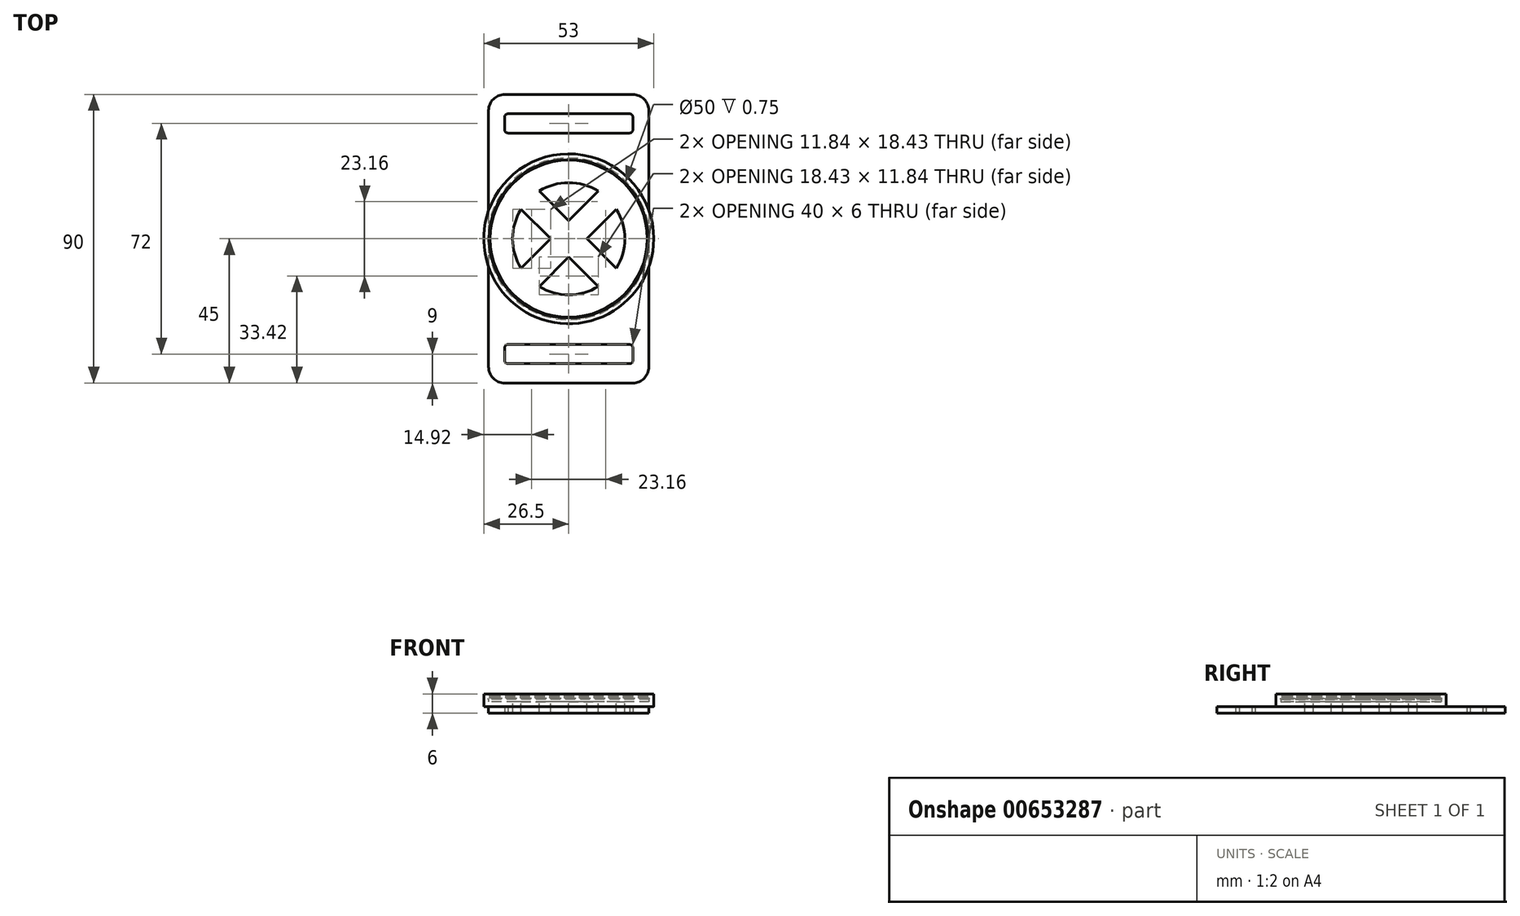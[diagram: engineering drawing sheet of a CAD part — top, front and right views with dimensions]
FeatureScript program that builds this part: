
annotation { "Feature Type Name" : "Feature", "Feature Type Description" : "" }
export const myFeature = defineFeature(function(context is Context, id is Id, definition is map)
    precondition{}
    {
        {
            var Q0;
            Q0=qCreatedBy(makeId("Top.planeOp"),FACE);
            var sketch = newSketch(context, id + "F0", { "sketchPlane" : qUnion([Q0])});
            skLineSegment(sketch, "E0.bottom", {"start": v(-25, 45) * mm, "end": v(25, 45) * mm});
            skLineSegment(sketch, "E0.top", {"start": v(-25, -45) * mm, "end": v(25, -45) * mm});
            skLineSegment(sketch, "E0.left", {"start": v(-25, 45) * mm, "end": v(-25, -45) * mm});
            skLineSegment(sketch, "E0.right", {"start": v(25, 45) * mm, "end": v(25, -45) * mm});
            skLineSegment(sketch, "E1", {"start": v(-25, 0) * mm, "end": v(25, 0) * mm, "construction": true});
            skLineSegment(sketch, "E2", {"start": v(0, -45) * mm, "end": v(0, 45) * mm, "construction": true});
            skPoint(sketch, "E3", {"position": v(0, 0) * mm});
            skSolve(sketch);
        }
        {
            var Q0;
            Q0=qSketchRegion(id+"F0",true);
            extrude(context, id + "F1", {"entities" : qUnion([Q0]), "depth" : 2 * mm, "offsetDistance" : 25 * mm});
        }
        {
            var Q0;
            Q0=makeQuery(id+"F1.opExtrude","CAP_FACE",FACE,{"disambiguationData":[OSD([sQuery(id+"F0.wireOp",EDGE,"E0.bottom"),sQuery(id+"F0.wireOp",EDGE,"E0.top"),sQuery(id+"F0.wireOp",EDGE,"E0.left"),sQuery(id+"F0.wireOp",EDGE,"E0.right")])],"isStart":false});
            var sketch = newSketch(context, id + "F2", { "sketchPlane" : qUnion([Q0])});
            skCircle(sketch, "E4", {"center": v(0, 0) * mm, "radius": 26.5 * mm});
            skSolve(sketch);
        }
        {
            var Q0;
            Q0=qSketchRegion(id+"F2",true);
            extrude(context, id + "F3", {"entities" : qUnion([Q0]), "operationType" : NewBodyOperationType.ADD, "depth" : 1.5 * mm, "offsetDistance" : 25 * mm});
        }
        {
            var Q0;
            Q0=makeQuery(id+"F3.opExtrude","CAP_FACE",FACE,{"disambiguationData":[OSD([sQuery(id+"F2.wireOp",EDGE,"E4")])],"isStart":false});
            var sketch = newSketch(context, id + "F4", { "sketchPlane" : qUnion([Q0])});
            skCircle(sketch, "E5", {"center": v(0, 0) * mm, "radius": 25 * mm});
            skSolve(sketch);
        }
        {
            var Q0;
            Q0=makeQuery(id+"F4.imprint","IMPRINT",FACE,{"disambiguationData":[TD([[makeQuery(id+"F4.imprint","IMPRINT",EDGE,{"derivedFrom":sQuery(id+"F4.wireOp",EDGE,"E5")}),-1.0]])]});
            extrude(context, id + "F5", {"entities" : qUnion([Q0]), "operationType" : NewBodyOperationType.ADD, "depth" : 1 * mm, "offsetDistance" : 25 * mm});
        }
        {
            var Q0;
            Q0=makeQuery(id+"F1.opExtrude","CAP_FACE",FACE,{"disambiguationData":[OSD([sQuery(id+"F0.wireOp",EDGE,"E0.bottom"),sQuery(id+"F0.wireOp",EDGE,"E0.top"),sQuery(id+"F0.wireOp",EDGE,"E0.left"),sQuery(id+"F0.wireOp",EDGE,"E0.right")])],"isStart":true});
            var sketch = newSketch(context, id + "F6", { "sketchPlane" : qUnion([Q0])});
            skLineSegment(sketch, "E6.bottom", {"start": v(-25, 35) * mm, "end": v(-22, 35) * mm});
            skLineSegment(sketch, "E6.top", {"start": v(-25, -35) * mm, "end": v(-22, -35) * mm});
            skLineSegment(sketch, "E6.left", {"start": v(-25, 35) * mm, "end": v(-25, -35) * mm});
            skLineSegment(sketch, "E6.right", {"start": v(-22, 35) * mm, "end": v(-22, -35) * mm});
            skLineSegment(sketch, "E7.bottom", {"start": v(22, 35) * mm, "end": v(25, 35) * mm});
            skLineSegment(sketch, "E7.top", {"start": v(22, -35) * mm, "end": v(25, -35) * mm});
            skLineSegment(sketch, "E7.left", {"start": v(22, 35) * mm, "end": v(22, -35) * mm});
            skLineSegment(sketch, "E7.right", {"start": v(25, 35) * mm, "end": v(25, -35) * mm});
            skSolve(sketch);
        }
        {
            var Q0;
            Q0=makeQuery(id+"F6.imprint","IMPRINT",FACE,{"disambiguationData":[TD([[makeQuery(id+"F6.imprint","IMPRINT",EDGE,{"derivedFrom":sQuery(id+"F6.wireOp",EDGE,"E6.bottom")}),-1.0]])]});
            var Q1;
            Q1=makeQuery(id+"F6.imprint","IMPRINT",FACE,{"disambiguationData":[TD([[makeQuery(id+"F6.imprint","IMPRINT",EDGE,{"derivedFrom":sQuery(id+"F6.wireOp",EDGE,"E7.bottom")}),-1.0]])]});
            extrude(context, id + "F7", {"entities" : qUnion([Q0, Q1]), "operationType" : NewBodyOperationType.ADD, "depth" : 3 * mm, "offsetDistance" : 25 * mm});
        }
        {
            var Q0;
            {var subQ0=sQuery(id+"F6.wireOp",EDGE,"E6.right");var subQ2=sQuery(id+"F6.wireOp",EDGE,"E6.left");var subQ3=sQuery(id+"F6.wireOp",EDGE,"E6.top");Q0=makeQuery(id+"Fcp3DyhTEGZhcjd_1.boolean.opBoolean","SPLIT",FACE,{"disambiguationData":[TD([makeQuery(id+"F7.opExtrude","SWEPT_FACE",FACE,{"disambiguationData":[OSD([subQ3])]})])],"derivedFrom":makeQuery(id+"F7.opExtrude","CAP_FACE",FACE,{"disambiguationData":[OSD([sQuery(id+"F6.wireOp",EDGE,"E6.bottom"),subQ3,subQ2,subQ0])],"isStart":false})});}
            var Q1;
            {var subQ0=sQuery(id+"F6.wireOp",EDGE,"E7.right");var subQ1=sQuery(id+"F6.wireOp",EDGE,"E7.left");var subQ2=sQuery(id+"F6.wireOp",EDGE,"E7.top");Q1=makeQuery(id+"Fcp3DyhTEGZhcjd_1.boolean.opBoolean","SPLIT",FACE,{"disambiguationData":[TD([makeQuery(id+"F7.opExtrude","SWEPT_FACE",FACE,{"disambiguationData":[OSD([subQ2])]})])],"derivedFrom":makeQuery(id+"F7.opExtrude","CAP_FACE",FACE,{"disambiguationData":[OSD([sQuery(id+"F6.wireOp",EDGE,"E7.bottom"),subQ2,subQ1,subQ0])],"isStart":false})});}
            var Q2;
            {var subQ0=sQuery(id+"F6.wireOp",EDGE,"E6.left");var subQ1=sQuery(id+"F6.wireOp",EDGE,"E6.right");var subQ3=sQuery(id+"F6.wireOp",EDGE,"E6.bottom");Q2=makeQuery(id+"Fcp3DyhTEGZhcjd_1.boolean.opBoolean","SPLIT",FACE,{"disambiguationData":[TD([makeQuery(id+"F7.opExtrude","SWEPT_FACE",FACE,{"disambiguationData":[OSD([subQ3])]})])],"derivedFrom":makeQuery(id+"F7.opExtrude","CAP_FACE",FACE,{"disambiguationData":[OSD([subQ3,sQuery(id+"F6.wireOp",EDGE,"E6.top"),subQ0,subQ1])],"isStart":false})});}
            var Q3;
            {var subQ0=sQuery(id+"F6.wireOp",EDGE,"E7.left");var subQ1=sQuery(id+"F6.wireOp",EDGE,"E7.right");var subQ2=sQuery(id+"F6.wireOp",EDGE,"E7.bottom");Q3=makeQuery(id+"Fcp3DyhTEGZhcjd_1.boolean.opBoolean","SPLIT",FACE,{"disambiguationData":[TD([makeQuery(id+"F7.opExtrude","SWEPT_FACE",FACE,{"disambiguationData":[OSD([subQ2])]})])],"derivedFrom":makeQuery(id+"F7.opExtrude","CAP_FACE",FACE,{"disambiguationData":[OSD([subQ2,sQuery(id+"F6.wireOp",EDGE,"E7.top"),subQ0,subQ1])],"isStart":false})});}
            var Q4;
            Q4=makeQuery(id+"F1.opExtrude","CAP_FACE",FACE,{"disambiguationData":[OSD([sQuery(id+"F0.wireOp",EDGE,"E0.bottom"),sQuery(id+"F0.wireOp",EDGE,"E0.top"),sQuery(id+"F0.wireOp",EDGE,"E0.left"),sQuery(id+"F0.wireOp",EDGE,"E0.right")])],"isStart":true});
            extrude(context, id + "F8", {"entities" : qUnion([Q0, Q1, Q2, Q3]), "operationType" : NewBodyOperationType.REMOVE, "endBound" : BoundingType.UP_TO_SURFACE, "oppositeDirection" : true, "depth" : 25 * mm, "endBoundEntityFace" : qUnion([Q4]), "offsetDistance" : 25 * mm});
        }
        {
            var Q0;
            Q0=makeQuery(id+"F3.opExtrude","CAP_FACE",FACE,{"disambiguationData":[OSD([sQuery(id+"F2.wireOp",EDGE,"E4")])],"isStart":false});
            var sketch = newSketch(context, id + "F9", { "sketchPlane" : qUnion([Q0])});
            skCircle(sketch, "E8", {"center": v(0, 0) * mm, "radius": 17.5 * mm});
            skLineSegment(sketch, "E9", {"start": v(14.88, -9.22) * mm, "end": v(5.66, 0) * mm});
            skLineSegment(sketch, "E10", {"start": v(-14.88, 9.22) * mm, "end": v(-5.66, 0) * mm});
            skLineSegment(sketch, "E11", {"start": v(14.88, 9.22) * mm, "end": v(5.66, 0) * mm});
            skLineSegment(sketch, "E12", {"start": v(-14.88, -9.22) * mm, "end": v(-5.66, 0) * mm});
            skLineSegment(sketch, "E13.trimOffspring", {"start": v(0, -5.66) * mm, "end": v(9.22, -14.88) * mm});
            skLineSegment(sketch, "E14.trimOffspring", {"start": v(0, 5.66) * mm, "end": v(9.22, 14.88) * mm});
            skLineSegment(sketch, "E15.trimOffspring", {"start": v(0, 5.66) * mm, "end": v(-9.22, 14.88) * mm});
            skLineSegment(sketch, "E16.trimOffspring", {"start": v(0, -5.66) * mm, "end": v(-9.22, -14.88) * mm});
            skLineSegment(sketch, "E17", {"start": v(0, 5.66) * mm, "end": v(0, 0) * mm, "construction": true});
            skLineSegment(sketch, "E18", {"start": v(-5.66, 0) * mm, "end": v(0, 0) * mm, "construction": true});
            skLineSegment(sketch, "E19", {"start": v(5.66, 0) * mm, "end": v(0, 0) * mm, "construction": true});
            skLineSegment(sketch, "E20", {"start": v(0, 0) * mm, "end": v(0, -5.66) * mm, "construction": true});
            skSolve(sketch);
        }
        {
            var Q0;
            {var subQ0=sQuery(id+"F9.wireOp",EDGE,"E10");Q0=makeQuery(id+"F9.imprint","IMPRINT",FACE,{"disambiguationData":[TD([[makeQuery(id+"F9.imprint","IMPRINT",EDGE,{"derivedFrom":subQ0}),-1.0]])]});}
            var Q1;
            {var subQ0=sQuery(id+"F9.wireOp",EDGE,"E13.trimOffspring");Q1=makeQuery(id+"F9.imprint","IMPRINT",FACE,{"disambiguationData":[TD([[makeQuery(id+"F9.imprint","IMPRINT",EDGE,{"derivedFrom":subQ0}),-1.0]])]});}
            var Q2;
            {var subQ0=sQuery(id+"F9.wireOp",EDGE,"E9");Q2=makeQuery(id+"F9.imprint","IMPRINT",FACE,{"disambiguationData":[TD([[makeQuery(id+"F9.imprint","IMPRINT",EDGE,{"derivedFrom":subQ0}),-1.0]])]});}
            var Q3;
            {var subQ0=sQuery(id+"F9.wireOp",EDGE,"E14.trimOffspring");Q3=makeQuery(id+"F9.imprint","IMPRINT",FACE,{"disambiguationData":[TD([[makeQuery(id+"F9.imprint","IMPRINT",EDGE,{"derivedFrom":subQ0}),1.0]])]});}
            extrude(context, id + "F10", {"entities" : qUnion([Q0, Q1, Q2, Q3]), "operationType" : NewBodyOperationType.REMOVE, "oppositeDirection" : true, "depth" : 25 * mm, "offsetDistance" : 25 * mm});
        }
        {
            var Q0;
            {var subQ0=sQuery(id+"F0.wireOp",EDGE,"E0.right");var subQ1=sQuery(id+"F0.wireOp",EDGE,"E0.left");var subQ2=sQuery(id+"F0.wireOp",EDGE,"E0.top");var subQ3=sQuery(id+"F0.wireOp",EDGE,"E0.bottom");Q0=makeQuery(id+"F8.boolean.opBoolean","MERGE",FACE,{"derivedFrom":[makeQuery(id+"F1.opExtrude","CAP_FACE",FACE,{"disambiguationData":[OSD([subQ3,subQ2,subQ1,subQ0])],"isStart":true}),makeQuery(id+"F8.opExtrude","CAP_FACE",FACE,{"disambiguationData":[OSD([subQ3,subQ2,subQ1,subQ0]),OD(0.0)],"isStart":false}),makeQuery(id+"F8.opExtrude","CAP_FACE",FACE,{"disambiguationData":[OSD([subQ3,subQ2,subQ1,subQ0]),OD(1.0)],"isStart":false}),makeQuery(id+"F8.opExtrude","CAP_FACE",FACE,{"disambiguationData":[OSD([subQ3,subQ2,subQ1,subQ0]),OD(2.0)],"isStart":false}),makeQuery(id+"F8.opExtrude","CAP_FACE",FACE,{"disambiguationData":[OSD([subQ3,subQ2,subQ1,subQ0]),OD(3.0)],"isStart":false})]});}
            var sketch = newSketch(context, id + "F11", { "sketchPlane" : qUnion([Q0])});
            skLineSegment(sketch, "E21.bottom", {"start": v(19, 39) * mm, "end": v(-19, 39) * mm});
            skLineSegment(sketch, "E21.top", {"start": v(19, 33) * mm, "end": v(-19, 33) * mm});
            skLineSegment(sketch, "E21.left", {"start": v(20, 38) * mm, "end": v(20, 34) * mm});
            skLineSegment(sketch, "E21.right", {"start": v(-20, 38) * mm, "end": v(-20, 34) * mm});
            skLineSegment(sketch, "E22.bottom", {"start": v(19, -33) * mm, "end": v(-19, -33) * mm});
            skLineSegment(sketch, "E22.top", {"start": v(19, -39) * mm, "end": v(-19, -39) * mm});
            skLineSegment(sketch, "E22.left", {"start": v(20, -34) * mm, "end": v(20, -38) * mm});
            skLineSegment(sketch, "E22.right", {"start": v(-20, -34) * mm, "end": v(-20, -38) * mm});
            skPoint(sketch, "E23.visualSharp", {"position": v(20, 39) * mm});
            skArc(sketch, "E23.filletArc", {"start": v(20, 38) * mm, "mid": v(19.7, 38.7) * mm, "end": v(19, 39) * mm});
            skPoint(sketch, "E24.visualSharp", {"position": v(20, 33) * mm});
            skArc(sketch, "E24.filletArc", {"start": v(19, 33) * mm, "mid": v(19.7, 33.3) * mm, "end": v(20, 34) * mm});
            skPoint(sketch, "E25.visualSharp", {"position": v(-20, 33) * mm});
            skArc(sketch, "E25.filletArc", {"start": v(-20, 34) * mm, "mid": v(-19.7, 33.3) * mm, "end": v(-19, 33) * mm});
            skPoint(sketch, "E26.visualSharp", {"position": v(-20, 39) * mm});
            skArc(sketch, "E26.filletArc", {"start": v(-19, 39) * mm, "mid": v(-19.7, 38.7) * mm, "end": v(-20, 38) * mm});
            skPoint(sketch, "E27.visualSharp", {"position": v(-20, -33) * mm});
            skArc(sketch, "E27.filletArc", {"start": v(-19, -33) * mm, "mid": v(-19.7, -33.3) * mm, "end": v(-20, -34) * mm});
            skPoint(sketch, "E28.visualSharp", {"position": v(-20, -39) * mm});
            skArc(sketch, "E28.filletArc", {"start": v(-20, -38) * mm, "mid": v(-19.7, -38.7) * mm, "end": v(-19, -39) * mm});
            skPoint(sketch, "E29.visualSharp", {"position": v(20, -39) * mm});
            skArc(sketch, "E29.filletArc", {"start": v(19, -39) * mm, "mid": v(19.7, -38.7) * mm, "end": v(20, -38) * mm});
            skPoint(sketch, "E30.visualSharp", {"position": v(20, -33) * mm});
            skArc(sketch, "E30.filletArc", {"start": v(20, -34) * mm, "mid": v(19.7, -33.3) * mm, "end": v(19, -33) * mm});
            skLineSegment(sketch, "E31.bottom", {"start": v(-4, 39) * mm, "end": v(4, 39) * mm});
            skLineSegment(sketch, "E31.top", {"start": v(-4, 45) * mm, "end": v(4, 45) * mm});
            skLineSegment(sketch, "E31.left", {"start": v(-4, 39) * mm, "end": v(-4, 45) * mm});
            skLineSegment(sketch, "E31.right", {"start": v(4, 39) * mm, "end": v(4, 45) * mm});
            skLineSegment(sketch, "E32.bottom", {"start": v(4, -39) * mm, "end": v(-4, -39) * mm});
            skLineSegment(sketch, "E32.top", {"start": v(4, -45) * mm, "end": v(-4, -45) * mm});
            skLineSegment(sketch, "E32.left", {"start": v(4, -39) * mm, "end": v(4, -45) * mm});
            skLineSegment(sketch, "E32.right", {"start": v(-4, -39) * mm, "end": v(-4, -45) * mm});
            skSolve(sketch);
        }
        {
            var Q0;
            Q0=makeQuery(id+"F11.imprint","IMPRINT",FACE,{"disambiguationData":[TD([[makeQuery(id+"F11.imprint","IMPRINT",EDGE,{"derivedFrom":sQuery(id+"F11.wireOp",EDGE,"E32.bottom")}),1.0]])]});
            var Q1;
            Q1=makeQuery(id+"F11.imprint","IMPRINT",FACE,{"disambiguationData":[TD([[makeQuery(id+"F11.imprint","IMPRINT",EDGE,{"derivedFrom":sQuery(id+"F11.wireOp",EDGE,"E22.bottom")}),1.0]])]});
            var Q2;
            Q2=makeQuery(id+"F11.imprint","IMPRINT",FACE,{"disambiguationData":[TD([[makeQuery(id+"F11.imprint","IMPRINT",EDGE,{"derivedFrom":sQuery(id+"F11.wireOp",EDGE,"E31.bottom")}),1.0]])]});
            var Q3;
            Q3=makeQuery(id+"F11.imprint","IMPRINT",FACE,{"disambiguationData":[TD([[makeQuery(id+"F11.imprint","IMPRINT",EDGE,{"derivedFrom":sQuery(id+"F11.wireOp",EDGE,"E21.top")}),-1.0]])]});
            extrude(context, id + "F12", {"entities" : qUnion([Q0, Q1, Q2, Q3]), "operationType" : NewBodyOperationType.REMOVE, "oppositeDirection" : true, "depth" : 25 * mm, "offsetDistance" : 25 * mm});
        }
        {
            var Q0;
            Q0=makeQuery(id+"F12.boolean.opBoolean","COPY",EDGE,{"derivedFrom":makeQuery(id+"F12.opExtrude","SWEPT_EDGE",EDGE,{"disambiguationData":[OSD([sQuery(id+"F0.wireOp",EDGE,"E0.top"),sQuery(id+"F11.wireOp",EDGE,"E31.top"),sQuery(id+"F11.wireOp",EDGE,"E31.left")])]})});
            var Q1;
            Q1=makeQuery(id+"F12.boolean.opBoolean","COPY",EDGE,{"derivedFrom":makeQuery(id+"F12.opExtrude","SWEPT_EDGE",EDGE,{"disambiguationData":[OSD([sQuery(id+"F11.wireOp",EDGE,"E21.bottom"),sQuery(id+"F11.wireOp",EDGE,"E31.bottom"),sQuery(id+"F11.wireOp",EDGE,"E31.left")])]})});
            var Q2;
            Q2=makeQuery(id+"F12.boolean.opBoolean","COPY",EDGE,{"derivedFrom":makeQuery(id+"F12.opExtrude","SWEPT_EDGE",EDGE,{"disambiguationData":[OSD([sQuery(id+"F0.wireOp",EDGE,"E0.top"),sQuery(id+"F11.wireOp",EDGE,"E31.top"),sQuery(id+"F11.wireOp",EDGE,"E31.right")])]})});
            var Q3;
            Q3=makeQuery(id+"F12.boolean.opBoolean","COPY",EDGE,{"derivedFrom":makeQuery(id+"F12.opExtrude","SWEPT_EDGE",EDGE,{"disambiguationData":[OSD([sQuery(id+"F11.wireOp",EDGE,"E21.bottom"),sQuery(id+"F11.wireOp",EDGE,"E31.bottom"),sQuery(id+"F11.wireOp",EDGE,"E31.right")])]})});
            fillet(context, id + "F13", {"entities" : qUnion([Q0, Q1, Q2, Q3]), "radius" : 1 * mm, "tangentPropagation" : true, "allowEdgeOverflow" : false});
        }
        {
            var Q0;
            Q0=makeQuery(id+"F12.boolean.opBoolean","COPY",EDGE,{"derivedFrom":makeQuery(id+"F12.opExtrude","SWEPT_EDGE",EDGE,{"disambiguationData":[OSD([sQuery(id+"F0.wireOp",EDGE,"E0.bottom"),sQuery(id+"F11.wireOp",EDGE,"E32.top"),sQuery(id+"F11.wireOp",EDGE,"E32.left")])]})});
            var Q1;
            Q1=makeQuery(id+"F12.boolean.opBoolean","COPY",EDGE,{"derivedFrom":makeQuery(id+"F12.opExtrude","SWEPT_EDGE",EDGE,{"disambiguationData":[OSD([sQuery(id+"F11.wireOp",EDGE,"E22.top"),sQuery(id+"F11.wireOp",EDGE,"E32.bottom"),sQuery(id+"F11.wireOp",EDGE,"E32.left")])]})});
            var Q2;
            Q2=makeQuery(id+"F12.boolean.opBoolean","COPY",EDGE,{"derivedFrom":makeQuery(id+"F12.opExtrude","SWEPT_EDGE",EDGE,{"disambiguationData":[OSD([sQuery(id+"F0.wireOp",EDGE,"E0.bottom"),sQuery(id+"F11.wireOp",EDGE,"E32.top"),sQuery(id+"F11.wireOp",EDGE,"E32.right")])]})});
            var Q3;
            Q3=makeQuery(id+"F12.boolean.opBoolean","COPY",EDGE,{"derivedFrom":makeQuery(id+"F12.opExtrude","SWEPT_EDGE",EDGE,{"disambiguationData":[OSD([sQuery(id+"F11.wireOp",EDGE,"E22.top"),sQuery(id+"F11.wireOp",EDGE,"E32.bottom"),sQuery(id+"F11.wireOp",EDGE,"E32.right")])]})});
            fillet(context, id + "F14", {"entities" : qUnion([Q0, Q1, Q2, Q3]), "radius" : 1 * mm, "tangentPropagation" : true, "allowEdgeOverflow" : false});
        }
        {
            var Q0;
            Q0=makeQuery(id+"F1.opExtrude","SWEPT_EDGE",EDGE,{"disambiguationData":[OSD([sQuery(id+"F0.wireOp",EDGE,"E0.top"),sQuery(id+"F0.wireOp",EDGE,"E0.right")])]});
            var Q1;
            Q1=makeQuery(id+"F1.opExtrude","SWEPT_EDGE",EDGE,{"disambiguationData":[OSD([sQuery(id+"F0.wireOp",EDGE,"E0.bottom"),sQuery(id+"F0.wireOp",EDGE,"E0.right")])]});
            var Q2;
            Q2=makeQuery(id+"F1.opExtrude","SWEPT_EDGE",EDGE,{"disambiguationData":[OSD([sQuery(id+"F0.wireOp",EDGE,"E0.bottom"),sQuery(id+"F0.wireOp",EDGE,"E0.left")])]});
            var Q3;
            Q3=makeQuery(id+"F1.opExtrude","SWEPT_EDGE",EDGE,{"disambiguationData":[OSD([sQuery(id+"F0.wireOp",EDGE,"E0.top"),sQuery(id+"F0.wireOp",EDGE,"E0.left")])]});
            fillet(context, id + "F15", {"entities" : qUnion([Q0, Q1, Q2, Q3]), "radius" : 5 * mm, "tangentPropagation" : true, "allowEdgeOverflow" : false});
        }
        {
            var Q0;
            Q0=makeQuery(id+"F1.opExtrude","SWEPT_BODY",BODY,{"disambiguationData":[OSD([sQuery(id+"F0.wireOp",EDGE,"E0.bottom"),sQuery(id+"F0.wireOp",EDGE,"E0.top"),sQuery(id+"F0.wireOp",EDGE,"E0.left"),sQuery(id+"F0.wireOp",EDGE,"E0.right")])]});
            transform(context, id + "F16", {"entities" : qUnion([Q0]), "transformType" : TransformType.TRANSLATION_3D, "dx" : 72.1 * mm, "dy" : 0 * mm, "dz" : 0 * mm, "makeCopy" : true});
        }
        {
            var Q0;
            Q0=makeQuery(id+"F16.opPattern","COPY",BODY,{"derivedFrom":makeQuery(id+"F1.opExtrude","SWEPT_BODY",BODY,{"disambiguationData":[OSD([sQuery(id+"F0.wireOp",EDGE,"E0.bottom"),sQuery(id+"F0.wireOp",EDGE,"E0.top"),sQuery(id+"F0.wireOp",EDGE,"E0.left"),sQuery(id+"F0.wireOp",EDGE,"E0.right")])]}),"instanceName":"1"});
            deleteBodies(context, id + "F17", {"entities" : qUnion([Q0])});
        }
        {
            var Q0;
            Q0=makeQuery(id+"F5.opExtrude","CAP_EDGE",EDGE,{"disambiguationData":[OSD([sQuery(id+"F4.wireOp",EDGE,"E5")])],"isStart":false});
            chamfer(context, id + "F18", {"entities" : qUnion([Q0]), "width" : 0.25 * mm, "tangentPropagation" : true});
        }
        {
            var Q0;
            Q0=makeQuery(id+"F5.opExtrude","CAP_FACE",FACE,{"disambiguationData":[OSD([sQuery(id+"F2.wireOp",EDGE,"E4"),sQuery(id+"F4.wireOp",EDGE,"E5")])],"isStart":false});
            var sketch = newSketch(context, id + "F19", { "sketchPlane" : qUnion([Q0])});
            skCircle(sketch, "E33", {"center": v(0, 0) * mm, "radius": 24.5 * mm});
            skSolve(sketch);
        }
        {
            var Q0;
            Q0=makeQuery(id+"F19.imprint","IMPRINT",FACE,{"disambiguationData":[TD([[makeQuery(id+"F19.imprint","IMPRINT",EDGE,{"derivedFrom":sQuery(id+"F19.wireOp",EDGE,"E33")}),-1.0]])]});
            var Q1;
            {var subQ0=sQuery(id+"F2.wireOp",EDGE,"E4");Q1=makeQuery(id+"F19.imprint","IMPRINT",FACE,{"disambiguationData":[TD([[makeQuery(id+"F19.imprint","IMPRINT",EDGE,{"derivedFrom":makeQuery(id+"F5.opExtrude","CAP_EDGE",EDGE,{"disambiguationData":[OSD([subQ0])],"isStart":false})}),1.0]])]});}
            extrude(context, id + "F20", {"entities" : qUnion([Q0, Q1]), "operationType" : NewBodyOperationType.ADD, "depth" : 0.5 * mm, "offsetDistance" : 25 * mm});
        }
        {
            var Q0;
            Q0=makeQuery(id+"F20.opExtrude","CAP_EDGE",EDGE,{"disambiguationData":[OSD([sQuery(id+"F19.wireOp",EDGE,"E33")])],"isStart":true});
            var Q1;
            Q1=makeQuery(id+"F20.opExtrude","CAP_EDGE",EDGE,{"disambiguationData":[OSD([sQuery(id+"F19.wireOp",EDGE,"E33")])],"isStart":false});
            chamfer(context, id + "F21", {"entities" : qUnion([Q0, Q1]), "width" : 0.25 * mm, "tangentPropagation" : true});
        }
        {
            var Q0;
            Q0=makeQuery(id+"F20.opExtrude","CAP_FACE",FACE,{"disambiguationData":[OSD([sQuery(id+"F2.wireOp",EDGE,"E4"),sQuery(id+"F19.wireOp",EDGE,"E33")])],"isStart":false});
            var sketch = newSketch(context, id + "F22", { "sketchPlane" : qUnion([Q0])});
            skCircle(sketch, "E34", {"center": v(0, 0) * mm, "radius": 24.5 * mm});
            skSolve(sketch);
        }
        {
            var Q0;
            Q0=makeQuery(id+"F22.imprint","IMPRINT",FACE,{"disambiguationData":[TD([[makeQuery(id+"F22.imprint","IMPRINT",EDGE,{"derivedFrom":sQuery(id+"F22.wireOp",EDGE,"E34")}),-1.0]])]});
            var Q1;
            {var subQ0=sQuery(id+"F2.wireOp",EDGE,"E4");Q1=makeQuery(id+"F22.imprint","IMPRINT",FACE,{"disambiguationData":[TD([[makeQuery(id+"F22.imprint","IMPRINT",EDGE,{"derivedFrom":makeQuery(id+"F20.opExtrude","CAP_EDGE",EDGE,{"disambiguationData":[OSD([subQ0])],"isStart":false})}),1.0]])]});}
            extrude(context, id + "F23", {"entities" : qUnion([Q0, Q1]), "operationType" : NewBodyOperationType.ADD, "depth" : 0.5 * mm, "offsetDistance" : 25 * mm});
        }
        {
            var Q0;
            Q0=makeQuery(id+"F23.opExtrude","CAP_EDGE",EDGE,{"disambiguationData":[OSD([sQuery(id+"F22.wireOp",EDGE,"E34")])],"isStart":true});
            var Q1;
            Q1=makeQuery(id+"F23.opExtrude","CAP_EDGE",EDGE,{"disambiguationData":[OSD([sQuery(id+"F22.wireOp",EDGE,"E34")])],"isStart":false});
            chamfer(context, id + "F24", {"entities" : qUnion([Q0, Q1]), "width" : 0.25 * mm, "tangentPropagation" : true});
        }
        {
            var Q0;
            Q0=makeQuery(id+"F23.opExtrude","CAP_FACE",FACE,{"disambiguationData":[OSD([sQuery(id+"F2.wireOp",EDGE,"E4"),sQuery(id+"F22.wireOp",EDGE,"E34")])],"isStart":false});
            var sketch = newSketch(context, id + "F25", { "sketchPlane" : qUnion([Q0])});
            skCircle(sketch, "E35", {"center": v(0, 0) * mm, "radius": 24.5 * mm});
            skSolve(sketch);
        }
        {
            var Q0;
            Q0=makeQuery(id+"F25.imprint","IMPRINT",FACE,{"disambiguationData":[TD([[makeQuery(id+"F25.imprint","IMPRINT",EDGE,{"derivedFrom":sQuery(id+"F25.wireOp",EDGE,"E35")}),-1.0]])]});
            var Q1;
            {var subQ0=sQuery(id+"F2.wireOp",EDGE,"E4");Q1=makeQuery(id+"F25.imprint","IMPRINT",FACE,{"disambiguationData":[TD([[makeQuery(id+"F25.imprint","IMPRINT",EDGE,{"derivedFrom":makeQuery(id+"F23.opExtrude","CAP_EDGE",EDGE,{"disambiguationData":[OSD([subQ0])],"isStart":false})}),1.0]])]});}
            extrude(context, id + "F26", {"entities" : qUnion([Q0, Q1]), "operationType" : NewBodyOperationType.ADD, "depth" : 0.5 * mm, "offsetDistance" : 25 * mm});
        }
        {
            var Q0;
            Q0=makeQuery(id+"F26.opExtrude","CAP_EDGE",EDGE,{"disambiguationData":[OSD([sQuery(id+"F25.wireOp",EDGE,"E35")])],"isStart":false});
            var Q1;
            Q1=makeQuery(id+"F26.opExtrude","CAP_EDGE",EDGE,{"disambiguationData":[OSD([sQuery(id+"F25.wireOp",EDGE,"E35")])],"isStart":true});
            chamfer(context, id + "F27", {"entities" : qUnion([Q0, Q1]), "width" : 0.25 * mm, "tangentPropagation" : true});
        }
    });
